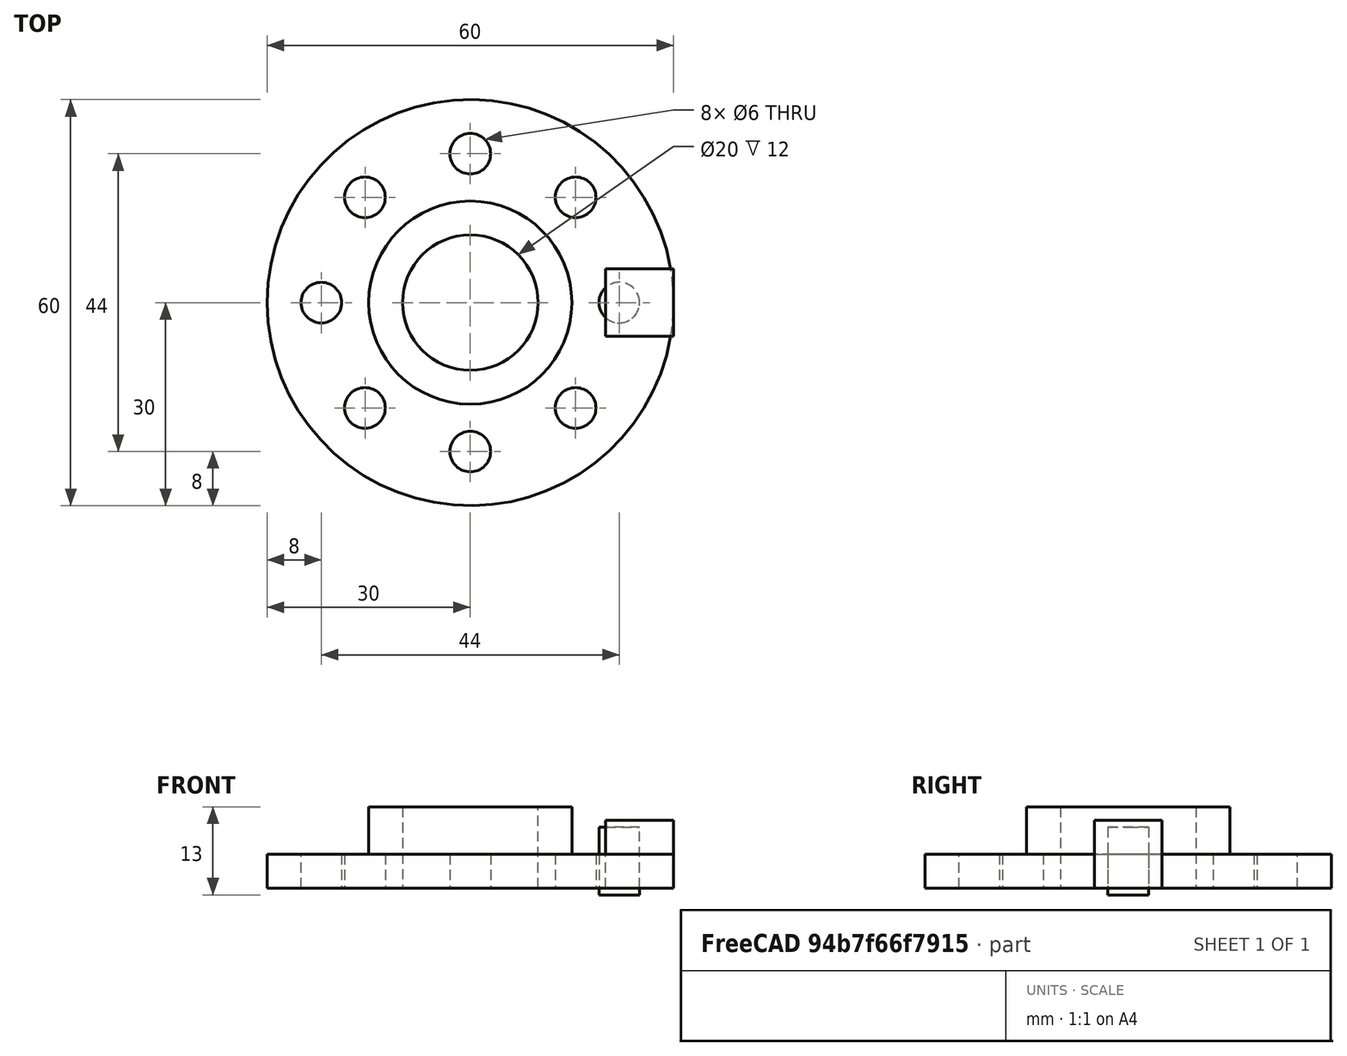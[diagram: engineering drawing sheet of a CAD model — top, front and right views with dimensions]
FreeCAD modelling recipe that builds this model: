
FCSTD DOCUMENT  (FreeCAD 0.21R33771 (Git))
Label: OJT1_T11P01_repeticions axials
License: All rights reserved
LicenseURL: http://en.wikipedia.org/wiki/All_rights_reserved
objects: Part::Cylinder×4, Part::FeaturePython×2, Part::Cut×2, Part::Box×1, Part::MultiFuse×1
note: 8 computed .brp shape members not serialized (recipe doc carries the construction recipe); baked Part::Feature solids carry a one-line shape summary decoded from their .brp

FEATURE [Part::Box] Box  label="Cube"
  AttacherType = Attacher::AttachEngine3D
  Height = 10
  Length = 10
  Placement = pos=(20,-5,0) rot=(0,0,1;0rad)
  Width = 10
FEATURE [Part::FeaturePython] Array  # Draft array (typed FeaturePython)
  AlwaysSyncPlacement = false
  Angle = 180
  ArrayType = 1
  Axis = (0,0,1)
  Base = -> Box
  Center = (0,0,1)
  Count = 6
  ExpandArray = false
  Fuse = false
  IntervalAxis = (0,0,0)
  IntervalX = (50,0,0)
  IntervalY = (0,50,0)
  IntervalZ = (0,0,50)
  NumberCircles = 3
  NumberPolar = 6
  NumberX = 2
  NumberY = 2
  NumberZ = 1
  PlacementList = 6 placements: [(20,-5,0),(19.1193,7.71062,1.11022e-16),(10.9356,17.476,0),(-1.42506,20.5662,0),(-13.2414,15.8008,1.11022e-16),(-20,5,0)]
  RadialDistance = 50
  ScaleList = (6) [(1,1,1),(1,1,1),(1,1,1),(1,1,1),(1,1,1),(1,1,1)]
  Symmetry = 1
  TangentialDistance = 25
FEATURE [Part::Cylinder] Cylinder  label="base"
  Angle = 360
  AttacherType = Attacher::AttachEngine3D
  FirstAngle = 0
  Height = 5
  Radius = 30
  SecondAngle = 0
FEATURE [Part::Cylinder] Cylinder001  label="tub_ext"
  Angle = 360
  AttacherType = Attacher::AttachEngine3D
  FirstAngle = 0
  Height = 12
  Radius = 15
  SecondAngle = 0
FEATURE [Part::MultiFuse] Fusion
  Refine = true
  Shapes = -> [Cylinder,Cylinder001]
FEATURE [Part::Cylinder] Cylinder002  label="tub_int"
  Angle = 360
  AttacherType = Attacher::AttachEngine3D
  FirstAngle = 0
  Height = 30
  Placement = pos=(0,0,-1) rot=(0,0,1;0rad)
  Radius = 10
  SecondAngle = 0
FEATURE [Part::Cut] Cut  label="brida sense els forats"
  Base = -> Fusion
  Refine = true
  Tool = -> Cylinder002
FEATURE [Part::Cylinder] Cylinder003  label="forat_origen"
  Angle = 360
  AttacherType = Attacher::AttachEngine3D
  FirstAngle = 0
  Height = 10
  Placement = pos=(22,0,-1) rot=(0,0,1;0rad)
  Radius = 3
  SecondAngle = 0
FEATURE [Part::FeaturePython] Array001  label="forats"  # Draft array (typed FeaturePython)
  AlwaysSyncPlacement = false
  Angle = 360
  ArrayType = 1
  Axis = (0,0,1)
  Base = -> Cylinder003
  Center = (0,0,1)
  Count = 8
  ExpandArray = false
  Fuse = false
  IntervalAxis = (0,0,0)
  IntervalX = (50,0,0)
  IntervalY = (0,50,0)
  IntervalZ = (0,0,50)
  NumberCircles = 3
  NumberPolar = 8
  NumberX = 2
  NumberY = 2
  NumberZ = 1
  PlacementList = 8 placements: [(22,0,-1),(15.5563,15.5563,-1),(4.88498e-15,22,-1),(-15.5563,15.5563,-1),(-22,2.69422e-15,-1),(-15.5563,-15.5563,-1),(-4.88498e-15,-22,-1),(15.5563,-15.5563,-1)]
  RadialDistance = 50
  ScaleList = (8) [(1,1,1),(1,1,1),(1,1,1),(1,1,1),(1,1,1),(1,1,1),(1,1,1),(1,1,1)]
  Symmetry = 1
  TangentialDistance = 25
FEATURE [Part::Cut] Cut001  label="brida"
  Base = -> Cut
  Refine = true
  Tool = -> Array001
